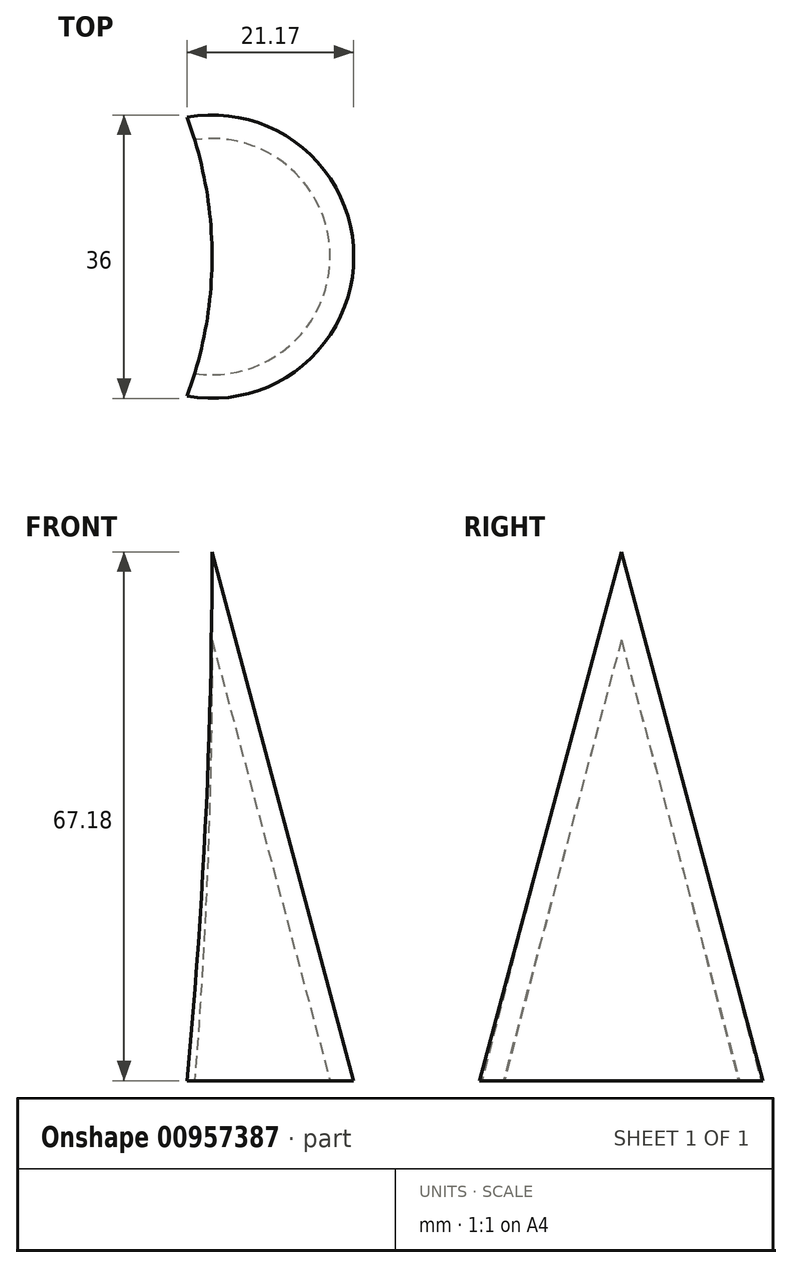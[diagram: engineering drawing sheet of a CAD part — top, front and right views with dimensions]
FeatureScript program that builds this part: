
annotation { "Feature Type Name" : "Feature", "Feature Type Description" : "" }
export const myFeature = defineFeature(function(context is Context, id is Id, definition is map)
    precondition{}
    {
        {
            var Q0;
            Q0=qCreatedBy(makeId("Front.planeOp"),FACE);
            var sketch = newSketch(context, id + "F0", { "sketchPlane" : qUnion([Q0])});
            skLineSegment(sketch, "E0", {"start": v(-15, 0) * mm, "end": v(-18, 0) * mm});
            skLineSegment(sketch, "E1", {"start": v(-18, 0) * mm, "end": v(0, 67.18) * mm});
            skLineSegment(sketch, "E2", {"start": v(0, 67.18) * mm, "end": v(0, 55.98) * mm});
            skLineSegment(sketch, "E3", {"start": v(0, 55.98) * mm, "end": v(-15, 0) * mm});
            skLineSegment(sketch, "E4", {"start": v(0, 0) * mm, "end": v(0, -11.34) * mm});
            skSolve(sketch);
        }
        {
            var Q0;
            Q0 = qSketchRegion(id + "F0", true);
            var Q1;
            Q1=sQuery(id+"F0.wireOp",EDGE,"E4");
            revolve(context, id + "F1", {"surfaceOperationType" : NewSurfaceOperationType.NEW, "entities" : qUnion([Q0]), "axis" : qUnion([Q1]), "revolveType" : RevolveType.FULL});
        }
        {
            var Q0;
            Q0=qCreatedBy(makeId("Front.planeOp"),FACE);
            var sketch = newSketch(context, id + "F2", { "sketchPlane" : qUnion([Q0])});
            skLineSegment(sketch, "E5", {"start": v(0, 0) * mm, "end": v(-51.1, 0) * mm});
            skLineSegment(sketch, "E6", {"start": v(-51.1, 0) * mm, "end": v(-51.1, 70) * mm});
            skLineSegment(sketch, "E7", {"start": v(-51.1, 70) * mm, "end": v(0, 70) * mm});
            skLineSegment(sketch, "E8", {"start": v(0, 70) * mm, "end": v(0, 0) * mm});
            skSolve(sketch);
        }
        {
            var Q0;
            Q0=makeQuery(id+"F2.imprint","IMPRINT",FACE,{"disambiguationData":[TD([[makeQuery(id+"F2.imprint","IMPRINT",EDGE,{"derivedFrom":sQuery(id+"F2.wireOp",EDGE,"E5")}),-1.0]])]});
            var Q1;
            Q1=sQuery(id+"F2.wireOp",EDGE,"E6");
            revolve(context, id + "F3", {"operationType" : NewBodyOperationType.REMOVE, "surfaceOperationType" : NewSurfaceOperationType.NEW, "entities" : qUnion([Q0]), "axis" : qUnion([Q1]), "revolveType" : RevolveType.FULL, "oppositeDirection" : true});
        }
    });
